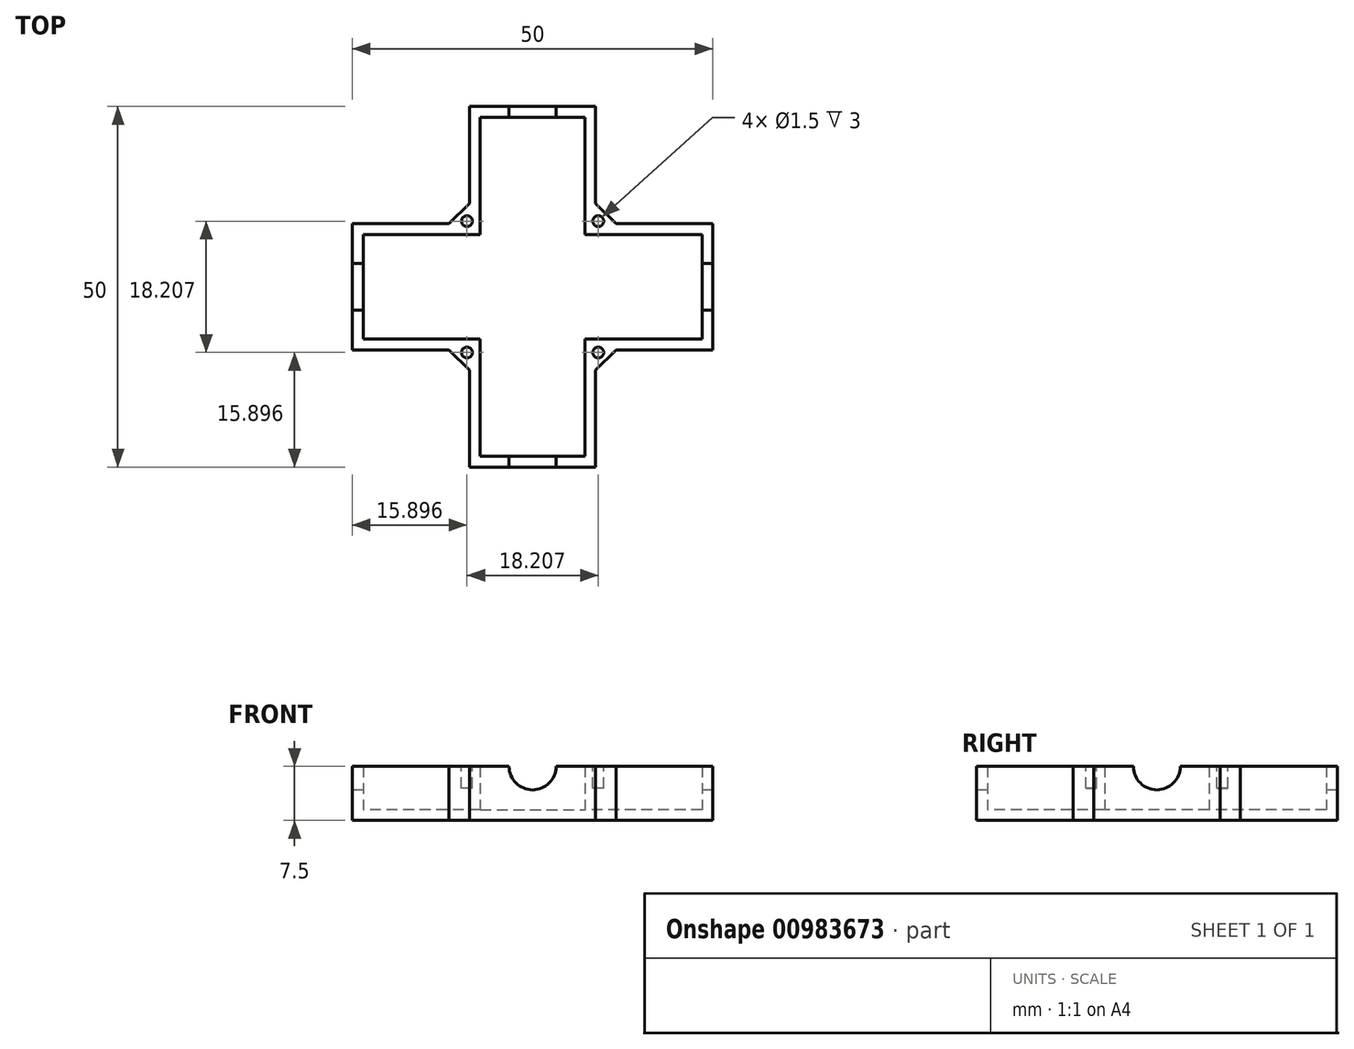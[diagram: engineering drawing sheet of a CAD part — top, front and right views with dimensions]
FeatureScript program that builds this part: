
annotation { "Feature Type Name" : "Feature", "Feature Type Description" : "" }
export const myFeature = defineFeature(function(context is Context, id is Id, definition is map)
    precondition{}
    {
        {
            var Q0;
            Q0=qCreatedBy(makeId("Top.planeOp"),FACE);
            var sketch = newSketch(context, id + "F0", { "sketchPlane" : qUnion([Q0])});
            skLineSegment(sketch, "E0.bottom", {"start": v(25, 8.75) * mm, "end": v(8.75, 8.75) * mm});
            skLineSegment(sketch, "E0.top", {"start": v(25, -8.75) * mm, "end": v(8.75, -8.75) * mm});
            skLineSegment(sketch, "E0.left", {"start": v(25, 8.75) * mm, "end": v(25, -8.75) * mm});
            skLineSegment(sketch, "E0.right", {"start": v(-25, 8.75) * mm, "end": v(-25, -8.75) * mm});
            skPoint(sketch, "E0.middle", {"position": v(0, 0) * mm});
            skLineSegment(sketch, "E1.bottom", {"start": v(-8.75, 25) * mm, "end": v(8.75, 25) * mm});
            skLineSegment(sketch, "E1.top", {"start": v(-8.75, -25) * mm, "end": v(8.75, -25) * mm});
            skLineSegment(sketch, "E1.left", {"start": v(-8.75, 25) * mm, "end": v(-8.75, 8.75) * mm});
            skLineSegment(sketch, "E1.right", {"start": v(8.75, 25) * mm, "end": v(8.75, 8.75) * mm});
            skLineSegment(sketch, "E2.trimOffspring", {"start": v(-8.75, 8.75) * mm, "end": v(-25, 8.75) * mm});
            skLineSegment(sketch, "E3.trimOffspring", {"start": v(-8.75, -8.75) * mm, "end": v(-8.75, -25) * mm});
            skLineSegment(sketch, "E4.trimOffspring", {"start": v(-8.75, -8.75) * mm, "end": v(-25, -8.75) * mm});
            skLineSegment(sketch, "E5.trimOffspring", {"start": v(8.75, -8.75) * mm, "end": v(8.75, -25) * mm});
            skSolve(sketch);
        }
        {
            var Q0;
            Q0 = qSketchRegion(id + "F0", true);
            extrude(context, id + "F1", {"entities" : qUnion([Q0]), "depth" : 7.5 * mm, "offsetDistance" : 25 * mm});
        }
        {
            var Q0;
            Q0=makeQuery(id+"F1.opExtrude","CAP_FACE",FACE,{"disambiguationData":[OSD([sQuery(id+"F0.wireOp",EDGE,"E0.bottom"),sQuery(id+"F0.wireOp",EDGE,"E0.top"),sQuery(id+"F0.wireOp",EDGE,"E0.left"),sQuery(id+"F0.wireOp",EDGE,"E0.right"),sQuery(id+"F0.wireOp",EDGE,"E1.bottom"),sQuery(id+"F0.wireOp",EDGE,"E1.top"),sQuery(id+"F0.wireOp",EDGE,"E1.left"),sQuery(id+"F0.wireOp",EDGE,"E1.right"),sQuery(id+"F0.wireOp",EDGE,"E2.trimOffspring"),sQuery(id+"F0.wireOp",EDGE,"E3.trimOffspring"),sQuery(id+"F0.wireOp",EDGE,"E4.trimOffspring"),sQuery(id+"F0.wireOp",EDGE,"E5.trimOffspring")])],"isStart":false});
            shell(context, id + "F2", {"entities" : qUnion([Q0]), "thickness" : 1.5 * mm});
        }
        {
            var Q0;
            Q0=makeQuery(id+"F1.opExtrude","CAP_FACE",FACE,{"disambiguationData":[OSD([sQuery(id+"F0.wireOp",EDGE,"E0.bottom"),sQuery(id+"F0.wireOp",EDGE,"E0.top"),sQuery(id+"F0.wireOp",EDGE,"E0.left"),sQuery(id+"F0.wireOp",EDGE,"E0.right"),sQuery(id+"F0.wireOp",EDGE,"E1.bottom"),sQuery(id+"F0.wireOp",EDGE,"E1.top"),sQuery(id+"F0.wireOp",EDGE,"E1.left"),sQuery(id+"F0.wireOp",EDGE,"E1.right"),sQuery(id+"F0.wireOp",EDGE,"E2.trimOffspring"),sQuery(id+"F0.wireOp",EDGE,"E3.trimOffspring"),sQuery(id+"F0.wireOp",EDGE,"E4.trimOffspring"),sQuery(id+"F0.wireOp",EDGE,"E5.trimOffspring")])],"isStart":false});
            var sketch = newSketch(context, id + "F3", { "sketchPlane" : qUnion([Q0])});
            skLineSegment(sketch, "E6", {"start": v(-11.58, 8.75) * mm, "end": v(-8.75, 11.58) * mm});
            skLineSegment(sketch, "E7", {"start": v(-8.75, 11.58) * mm, "end": v(-8.75, 8.75) * mm});
            skLineSegment(sketch, "E8", {"start": v(-8.75, 8.75) * mm, "end": v(-11.58, 8.75) * mm});
            skLineSegment(sketch, "E9", {"start": v(0, 0) * mm, "end": v(0, 7.25) * mm});
            skLineSegment(sketch, "E10", {"start": v(0, 0) * mm, "end": v(7.25, 0) * mm});
            skLineSegment(sketch, "E11.MirrorCS", {"start": v(8.75, 8.75) * mm, "end": v(11.58, 8.75) * mm});
            skLineSegment(sketch, "E12.MirrorCS", {"start": v(11.58, 8.75) * mm, "end": v(8.75, 11.58) * mm});
            skLineSegment(sketch, "E13.MirrorCS", {"start": v(8.75, 11.58) * mm, "end": v(8.75, 8.75) * mm});
            skLineSegment(sketch, "E14.MirrorCS", {"start": v(-8.75, -8.75) * mm, "end": v(-11.58, -8.75) * mm});
            skLineSegment(sketch, "E15.MirrorCS", {"start": v(8.75, -8.75) * mm, "end": v(11.58, -8.75) * mm});
            skLineSegment(sketch, "E16.MirrorCS", {"start": v(-8.75, -11.58) * mm, "end": v(-8.75, -8.75) * mm});
            skLineSegment(sketch, "E17.MirrorCS", {"start": v(11.58, -8.75) * mm, "end": v(8.75, -11.58) * mm});
            skLineSegment(sketch, "E18.MirrorCS", {"start": v(8.75, -11.58) * mm, "end": v(8.75, -8.75) * mm});
            skLineSegment(sketch, "E19.MirrorCS", {"start": v(-11.58, -8.75) * mm, "end": v(-8.75, -11.58) * mm});
            skSolve(sketch);
        }
        {
            var Q0;
            Q0 = qSketchRegion(id + "F3", true);
            var Q1;
            Q1=makeQuery(id+"F1.opExtrude","CAP_FACE",FACE,{"disambiguationData":[OSD([sQuery(id+"F0.wireOp",EDGE,"E0.bottom"),sQuery(id+"F0.wireOp",EDGE,"E0.top"),sQuery(id+"F0.wireOp",EDGE,"E0.left"),sQuery(id+"F0.wireOp",EDGE,"E0.right"),sQuery(id+"F0.wireOp",EDGE,"E1.bottom"),sQuery(id+"F0.wireOp",EDGE,"E1.top"),sQuery(id+"F0.wireOp",EDGE,"E1.left"),sQuery(id+"F0.wireOp",EDGE,"E1.right"),sQuery(id+"F0.wireOp",EDGE,"E2.trimOffspring"),sQuery(id+"F0.wireOp",EDGE,"E3.trimOffspring"),sQuery(id+"F0.wireOp",EDGE,"E4.trimOffspring"),sQuery(id+"F0.wireOp",EDGE,"E5.trimOffspring")])],"isStart":true});
            extrude(context, id + "F4", {"entities" : qUnion([Q0]), "operationType" : NewBodyOperationType.ADD, "endBound" : BoundingType.UP_TO_SURFACE, "oppositeDirection" : true, "depth" : 25 * mm, "endBoundEntityFace" : qUnion([Q1]), "offsetDistance" : 25 * mm});
        }
        {
            var Q0;
            Q0=makeQuery(id+"F4.boolean.opBoolean","MERGE",FACE,{"derivedFrom":[makeQuery(id+"F1.opExtrude","CAP_FACE",FACE,{"disambiguationData":[OSD([sQuery(id+"F0.wireOp",EDGE,"E0.bottom"),sQuery(id+"F0.wireOp",EDGE,"E0.top"),sQuery(id+"F0.wireOp",EDGE,"E0.left"),sQuery(id+"F0.wireOp",EDGE,"E0.right"),sQuery(id+"F0.wireOp",EDGE,"E1.bottom"),sQuery(id+"F0.wireOp",EDGE,"E1.top"),sQuery(id+"F0.wireOp",EDGE,"E1.left"),sQuery(id+"F0.wireOp",EDGE,"E1.right"),sQuery(id+"F0.wireOp",EDGE,"E2.trimOffspring"),sQuery(id+"F0.wireOp",EDGE,"E3.trimOffspring"),sQuery(id+"F0.wireOp",EDGE,"E4.trimOffspring"),sQuery(id+"F0.wireOp",EDGE,"E5.trimOffspring")])],"isStart":false}),makeQuery(id+"F4.opExtrude","CAP_FACE",FACE,{"disambiguationData":[OSD([sQuery(id+"F3.wireOp",EDGE,"E6"),sQuery(id+"F3.wireOp",EDGE,"E7"),sQuery(id+"F3.wireOp",EDGE,"E8")])],"isStart":true}),makeQuery(id+"F4.opExtrude","CAP_FACE",FACE,{"disambiguationData":[OSD([sQuery(id+"F3.wireOp",EDGE,"E11.MirrorCS"),sQuery(id+"F3.wireOp",EDGE,"E12.MirrorCS"),sQuery(id+"F3.wireOp",EDGE,"E13.MirrorCS")])],"isStart":true}),makeQuery(id+"F4.opExtrude","CAP_FACE",FACE,{"disambiguationData":[OSD([sQuery(id+"F3.wireOp",EDGE,"E14.MirrorCS"),sQuery(id+"F3.wireOp",EDGE,"E16.MirrorCS"),sQuery(id+"F3.wireOp",EDGE,"E19.MirrorCS")])],"isStart":true}),makeQuery(id+"F4.opExtrude","CAP_FACE",FACE,{"disambiguationData":[OSD([sQuery(id+"F3.wireOp",EDGE,"E15.MirrorCS"),sQuery(id+"F3.wireOp",EDGE,"E17.MirrorCS"),sQuery(id+"F3.wireOp",EDGE,"E18.MirrorCS")])],"isStart":true})]});
            var sketch = newSketch(context, id + "F5", { "sketchPlane" : qUnion([Q0])});
            skCircle(sketch, "E20", {"center": v(-9.1, 9.1) * mm, "radius": 0.75 * mm});
            skCircle(sketch, "E21", {"center": v(9.1, 9.1) * mm, "radius": 0.75 * mm});
            skCircle(sketch, "E22", {"center": v(9.1, -9.1) * mm, "radius": 0.75 * mm});
            skCircle(sketch, "E23", {"center": v(-9.1, -9.1) * mm, "radius": 0.75 * mm});
            skLineSegment(sketch, "E24", {"start": v(-9.1, 9.1) * mm, "end": v(-10.16, 10.16) * mm});
            skLineSegment(sketch, "E25", {"start": v(9.1, 9.1) * mm, "end": v(10.16, 10.16) * mm});
            skLineSegment(sketch, "E26", {"start": v(9.1, -9.1) * mm, "end": v(10.16, -10.16) * mm});
            skPoint(sketch, "E26.endSnap0", {"position": v(10.16, -10.16) * mm});
            skLineSegment(sketch, "E27", {"start": v(-9.1, -9.1) * mm, "end": v(-10.16, -10.16) * mm});
            skPoint(sketch, "E27.endSnap0", {"position": v(-10.16, -10.16) * mm});
            skSolve(sketch);
        }
        {
            var Q0;
            Q0 = qSketchRegion(id + "F5", true);
            extrude(context, id + "F6", {"entities" : qUnion([Q0]), "operationType" : NewBodyOperationType.REMOVE, "oppositeDirection" : true, "depth" : 3 * mm, "offsetDistance" : 25 * mm});
        }
        {
            var Q0;
            Q0=makeQuery(id+"F1.opExtrude","SWEPT_FACE",FACE,{"disambiguationData":[OSD([sQuery(id+"F0.wireOp",EDGE,"E1.top")])]});
            var sketch = newSketch(context, id + "F7", { "sketchPlane" : qUnion([Q0])});
            skCircle(sketch, "E28", {"center": v(0, 7.5) * mm, "radius": 3.25 * mm});
            skSolve(sketch);
        }
        {
            var Q0;
            Q0 = qSketchRegion(id + "F7", true);
            extrude(context, id + "F8", {"entities" : qUnion([Q0]), "operationType" : NewBodyOperationType.REMOVE, "endBound" : BoundingType.THROUGH_ALL, "oppositeDirection" : true, "depth" : 25 * mm, "offsetDistance" : 25 * mm});
        }
        {
            var Q0;
            Q0=makeQuery(id+"F1.opExtrude","SWEPT_FACE",FACE,{"disambiguationData":[OSD([sQuery(id+"F0.wireOp",EDGE,"E0.right")])]});
            var sketch = newSketch(context, id + "F9", { "sketchPlane" : qUnion([Q0])});
            skCircle(sketch, "E29", {"center": v(0, 7.5) * mm, "radius": 3.25 * mm});
            skSolve(sketch);
        }
        {
            var Q0;
            Q0 = qSketchRegion(id + "F9", true);
            extrude(context, id + "F10", {"entities" : qUnion([Q0]), "operationType" : NewBodyOperationType.REMOVE, "endBound" : BoundingType.THROUGH_ALL, "oppositeDirection" : true, "depth" : 25 * mm, "offsetDistance" : 25 * mm});
        }
    });
